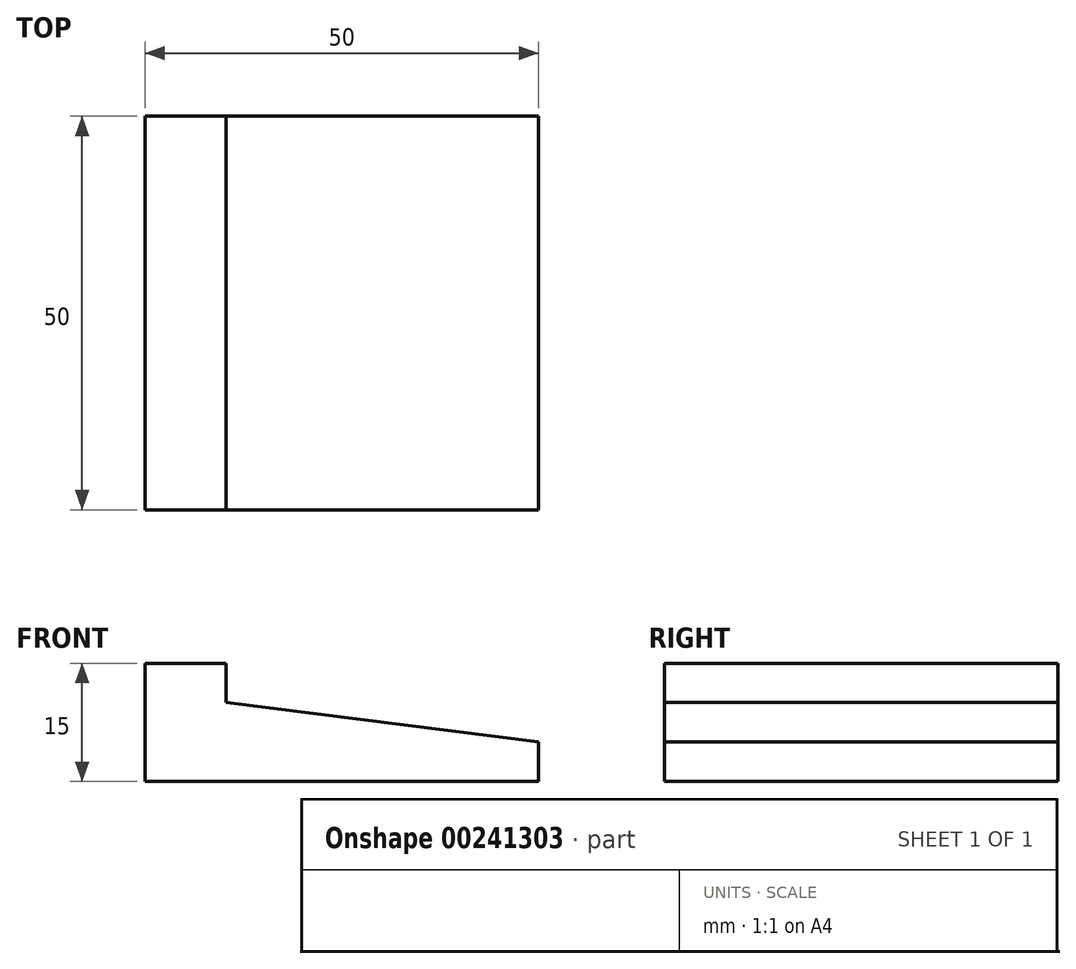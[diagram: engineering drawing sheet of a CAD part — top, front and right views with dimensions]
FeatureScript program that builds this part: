
annotation { "Feature Type Name" : "Feature", "Feature Type Description" : "" }
export const myFeature = defineFeature(function(context is Context, id is Id, definition is map)
    precondition{}
    {
        {
            var Q0;
            Q0=qCreatedBy(makeId("Top.planeOp"),FACE);
            var sketch = newSketch(context, id + "F0", { "sketchPlane" : qUnion([Q0])});
            skLineSegment(sketch, "E0.bottom", {"start": v(-82.6, 11.98) * mm, "end": v(-32.6, 11.98) * mm});
            skLineSegment(sketch, "E0.top", {"start": v(-82.6, -38.02) * mm, "end": v(-32.6, -38.02) * mm});
            skLineSegment(sketch, "E0.left", {"start": v(-82.6, 11.98) * mm, "end": v(-82.6, -38.02) * mm});
            skLineSegment(sketch, "E0.right", {"start": v(-32.6, 11.98) * mm, "end": v(-32.6, -38.02) * mm});
            skSolve(sketch);
        }
        {
            var Q0;
            Q0=makeQuery(id+"F0.imprint","IMPRINT",FACE,{"disambiguationData":[TD([[makeQuery(id+"F0.imprint","IMPRINT",EDGE,{"derivedFrom":sQuery(id+"F0.wireOp",EDGE,"E0.bottom")}),-1.0]])]});
            extrude(context, id + "F1", {"entities" : qUnion([Q0]), "depth" : 15 * mm});
        }
        {
            var Q0;
            Q0=makeQuery(id+"F1.opExtrude","SWEPT_FACE",FACE,{"disambiguationData":[OSD([sQuery(id+"F0.wireOp",EDGE,"E0.top")])]});
            var sketch = newSketch(context, id + "F2", { "sketchPlane" : qUnion([Q0])});
            skLineSegment(sketch, "E1", {"start": v(-72.3, 15) * mm, "end": v(-72.3, 10) * mm});
            skLineSegment(sketch, "E2", {"start": v(-32.6, 0) * mm, "end": v(-32.6, 5) * mm});
            skLineSegment(sketch, "E3", {"start": v(-72.3, 10) * mm, "end": v(-32.6, 5) * mm});
            skSolve(sketch);
        }
        {
            var Q0;
            Q0 = qSketchRegion(id + "F2", true);
            var Q1;
            {var subQ0=sQuery(id+"F2.wireOp",EDGE,"E1");Q1=makeQuery(id+"F2.imprint","IMPRINT",FACE,{"disambiguationData":[TD([[makeQuery(id+"F2.imprint","IMPRINT",EDGE,{"derivedFrom":subQ0}),1.0]])]});}
            extrude(context, id + "F3", {"entities" : qUnion([Q0, Q1]), "operationType" : NewBodyOperationType.REMOVE, "endBound" : BoundingType.THROUGH_ALL, "oppositeDirection" : true, "depth" : 25 * mm});
        }
    });
